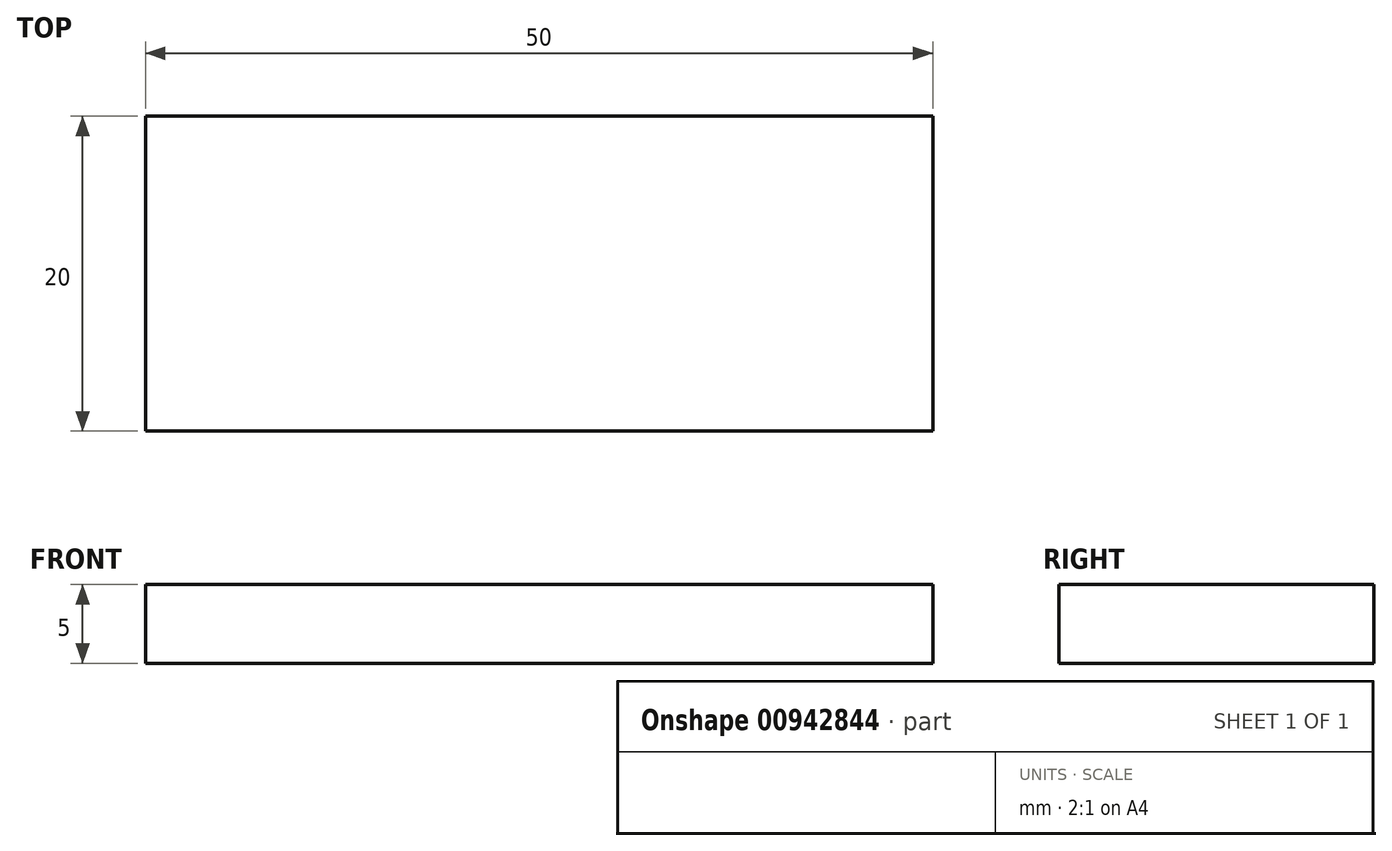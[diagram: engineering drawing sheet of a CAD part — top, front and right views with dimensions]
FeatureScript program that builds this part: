
annotation { "Feature Type Name" : "Feature", "Feature Type Description" : "" }
export const myFeature = defineFeature(function(context is Context, id is Id, definition is map)
    precondition{}
    {
        {
            var Q0;
            Q0=qCreatedBy(makeId("Top.planeOp"),FACE);
            var sketch = newSketch(context, id + "F0", { "sketchPlane" : qUnion([Q0])});
            skLineSegment(sketch, "E0.bottom", {"start": v(-18.64, 6.24) * mm, "end": v(31.36, 6.24) * mm});
            skLineSegment(sketch, "E0.top", {"start": v(-18.64, -13.76) * mm, "end": v(31.36, -13.76) * mm});
            skLineSegment(sketch, "E0.left", {"start": v(-18.64, 6.24) * mm, "end": v(-18.64, -13.76) * mm});
            skLineSegment(sketch, "E0.right", {"start": v(31.36, 6.24) * mm, "end": v(31.36, -13.76) * mm});
            skSolve(sketch);
        }
        {
            var Q0;
            Q0 = qSketchRegion(id + "F0", true);
            extrude(context, id + "F1", {"entities" : qUnion([Q0]), "depth" : 5 * mm, "offsetDistance" : 25 * mm});
        }
    });
